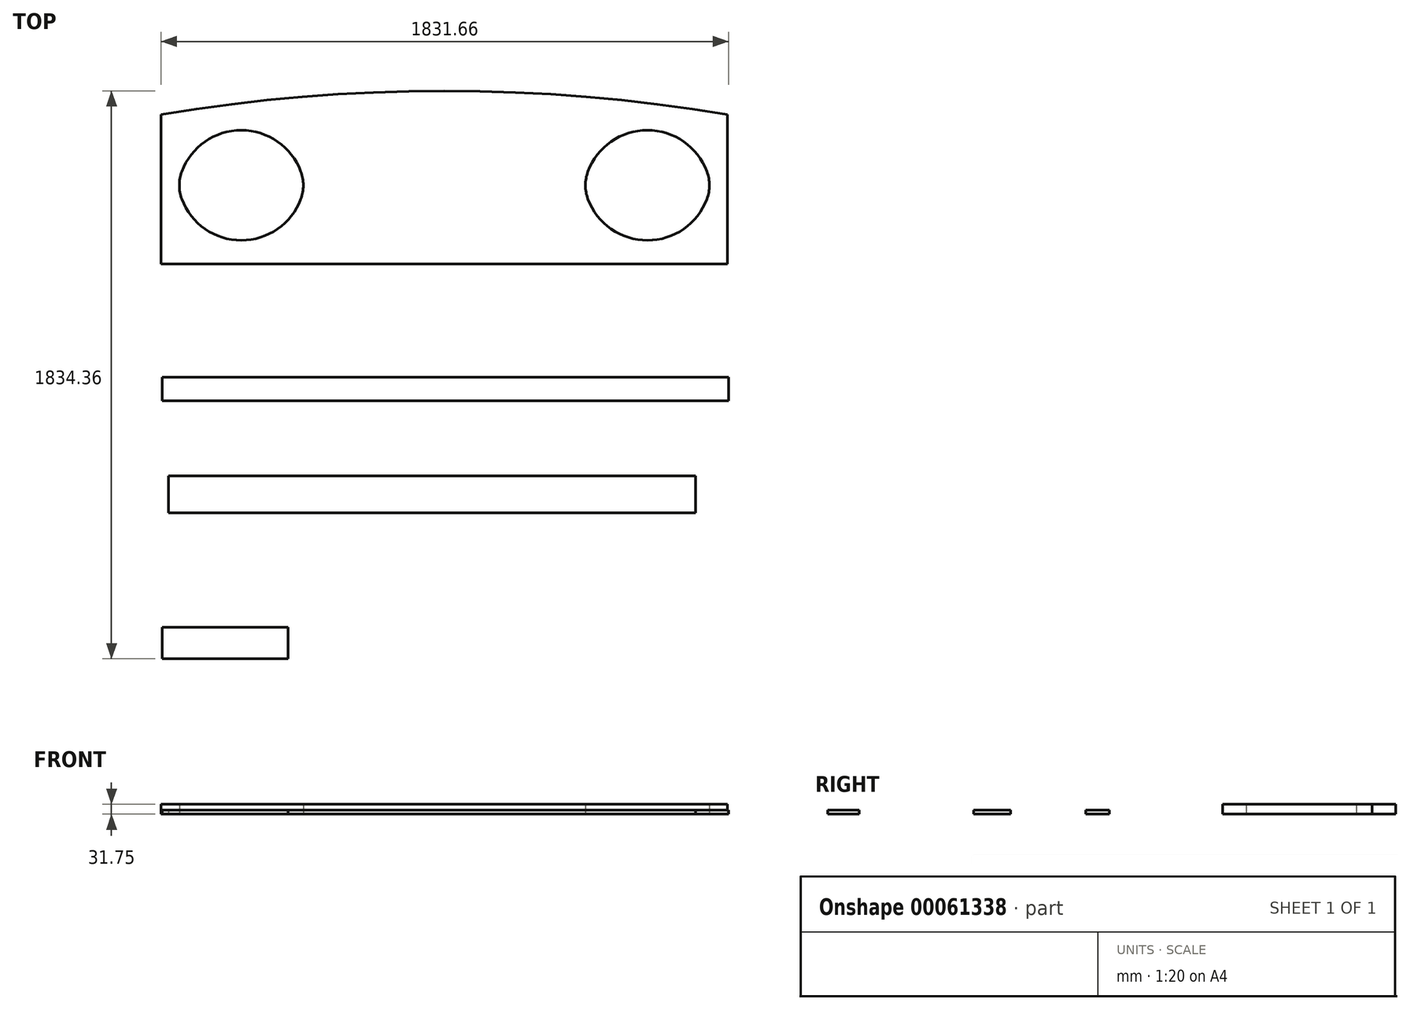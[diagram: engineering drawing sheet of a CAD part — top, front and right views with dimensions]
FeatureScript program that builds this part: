
annotation { "Feature Type Name" : "Feature", "Feature Type Description" : "" }
export const myFeature = defineFeature(function(context is Context, id is Id, definition is map)
    precondition{}
    {
        {
            var Q0;
            Q0=qCreatedBy(makeId("Top.planeOp"),FACE);
            var sketch = newSketch(context, id + "F0", { "sketchPlane" : qUnion([Q0])});
            skLineSegment(sketch, "E0", {"start": v(-914.4, 0) * mm, "end": v(914.4, 0) * mm});
            skLineSegment(sketch, "E1", {"start": v(-914.4, 0) * mm, "end": v(-914.4, 482.6) * mm});
            skLineSegment(sketch, "E2", {"start": v(914.4, 0) * mm, "end": v(914.4, 482.6) * mm});
            skArc(sketch, "E3", {"start": v(914.4, 482.6) * mm, "mid": v(0, 558.8) * mm, "end": v(-914.4, 482.6) * mm});
            skArc(sketch, "E4", {"start": v(-463.44, 298.3) * mm, "mid": v(-655.58, 431.8) * mm, "end": v(-847.71, 298.3) * mm});
            skArc(sketch, "E5", {"start": v(-847.71, 209.7) * mm, "mid": v(-655.58, 76.2) * mm, "end": v(-463.44, 209.7) * mm});
            skPoint(sketch, "E6.visualSharp", {"position": v(-858.78, 254) * mm});
            skArc(sketch, "E6.filletArc", {"start": v(-847.71, 298.3) * mm, "mid": v(-855.69, 254) * mm, "end": v(-847.71, 209.7) * mm});
            skPoint(sketch, "E7.visualSharp", {"position": v(-452.38, 254) * mm});
            skArc(sketch, "E7.filletArc", {"start": v(-463.44, 209.7) * mm, "mid": v(-455.46, 254) * mm, "end": v(-463.44, 298.3) * mm});
            skArc(sketch, "E8.MirrorCS", {"start": v(847.71, 298.3) * mm, "mid": v(855.69, 254) * mm, "end": v(847.71, 209.7) * mm});
            skArc(sketch, "E9.MirrorCS", {"start": v(847.71, 209.7) * mm, "mid": v(655.58, 76.2) * mm, "end": v(463.44, 209.7) * mm});
            skArc(sketch, "E10.MirrorCS", {"start": v(463.44, 209.7) * mm, "mid": v(455.46, 254) * mm, "end": v(463.44, 298.3) * mm});
            skArc(sketch, "E11.MirrorCS", {"start": v(463.44, 298.3) * mm, "mid": v(655.58, 431.8) * mm, "end": v(847.71, 298.3) * mm});
            skLineSegment(sketch, "E12.bottom", {"start": v(-911.54, -365.95) * mm, "end": v(917.26, -365.95) * mm});
            skLineSegment(sketch, "E12.top", {"start": v(-911.54, -442.15) * mm, "end": v(917.26, -442.15) * mm});
            skLineSegment(sketch, "E12.left", {"start": v(-911.54, -365.95) * mm, "end": v(-911.54, -442.15) * mm});
            skLineSegment(sketch, "E12.right", {"start": v(917.26, -365.95) * mm, "end": v(917.26, -442.15) * mm});
            skLineSegment(sketch, "E13.bottom", {"start": v(-891.07, -684.52) * mm, "end": v(810.73, -684.52) * mm});
            skLineSegment(sketch, "E13.top", {"start": v(-891.07, -803.52) * mm, "end": v(810.73, -803.52) * mm});
            skLineSegment(sketch, "E13.left", {"start": v(-891.07, -684.52) * mm, "end": v(-891.07, -803.52) * mm});
            skLineSegment(sketch, "E13.right", {"start": v(810.73, -684.52) * mm, "end": v(810.73, -803.52) * mm});
            skLineSegment(sketch, "E14.bottom", {"start": v(-911, -1173.96) * mm, "end": v(-504.6, -1173.96) * mm});
            skLineSegment(sketch, "E14.top", {"start": v(-911, -1275.56) * mm, "end": v(-504.6, -1275.56) * mm});
            skLineSegment(sketch, "E14.left", {"start": v(-911, -1173.96) * mm, "end": v(-911, -1275.56) * mm});
            skLineSegment(sketch, "E14.right", {"start": v(-504.6, -1173.96) * mm, "end": v(-504.6, -1275.56) * mm});
            skSolve(sketch);
        }
        {
            var Q0;
            Q0=makeQuery(id+"F0.imprint","IMPRINT",FACE,{"disambiguationData":[TD([[makeQuery(id+"F0.imprint","IMPRINT",EDGE,{"derivedFrom":sQuery(id+"F0.wireOp",EDGE,"E0")}),1.0]])]});
            extrude(context, id + "F1", {"entities" : qUnion([Q0]), "depth" : 31.75 * mm});
        }
        {
            var Q0;
            Q0=makeQuery(id+"F0.imprint","IMPRINT",FACE,{"disambiguationData":[TD([[makeQuery(id+"F0.imprint","IMPRINT",EDGE,{"derivedFrom":sQuery(id+"F0.wireOp",EDGE,"E12.bottom")}),-1.0]])]});
            var Q1;
            Q1=makeQuery(id+"F0.imprint","IMPRINT",FACE,{"disambiguationData":[TD([[makeQuery(id+"F0.imprint","IMPRINT",EDGE,{"derivedFrom":sQuery(id+"F0.wireOp",EDGE,"E13.bottom")}),-1.0]])]});
            var Q2;
            Q2=makeQuery(id+"F0.imprint","IMPRINT",FACE,{"disambiguationData":[TD([[makeQuery(id+"F0.imprint","IMPRINT",EDGE,{"derivedFrom":sQuery(id+"F0.wireOp",EDGE,"E14.bottom")}),-1.0]])]});
            extrude(context, id + "F2", {"entities" : qUnion([Q0, Q1, Q2]), "depth" : 12.7 * mm});
        }
    });
